# Revit family: Haworth_Very_Stool_Side4Leg_AP_PRELIMINARY
name_source: partatom
category: Furniture
revit_build: Autodesk Revit 2018 (Build: 20170223_1515(x64)
units: mm (PartAtom-declared; Revit-internal decimal feet)

## family parameters
Always vertical = Yes
Cut with Voids When Loaded = No
OmniClass Number = 23.40.70.14.64.21
OmniClass Title = Systems Furniture
Room Calculation Point = No
Shared = No
Work Plane-Based = No

## types (4) — shared parameters
Actual Depth = 559 mm
Actual Height = 1166 mm
Actual Width = 597 mm
Assembly Code = E2020200
Back Cushion = Yes
Back Finish = Haworth _ Polymer _ Glacier
Chair Finish = Haworth _ Polymer _ Glacier
Cushion Finish = Haworth _ Fabric _ Tellure _ Sky 3A-32
Description = Haworth - Very - Stool - Side
Frame Finish = Haworth _ Metal _ Chrome
Glide Finish = Haworth _ Polymer _ Slate
Manufacturer = Haworth
Model = SEVYGLXX
Revision Number = 4
Seat Cushion = Yes
Size = Verify Final Dim. w/ Haworth
Sustainability Info = https://www.haworth.com
URL = https://www.haworth.com
URL - Product = https://www.haworth.com
Warranty = http://www.haworth.com

## per-type parameters (varying)
| type | Arms | Tetro Back |
| Tetro Back without Arm | No | Yes |
| Tetro Back with Arms | Yes | Yes |
| Polymer Back with Arms | Yes | No |
| Polymer Back without Arm | No | No |

## geometry (parser evidence)
native form markers: Sweep x8
no freeform markers — native parametric forms only
